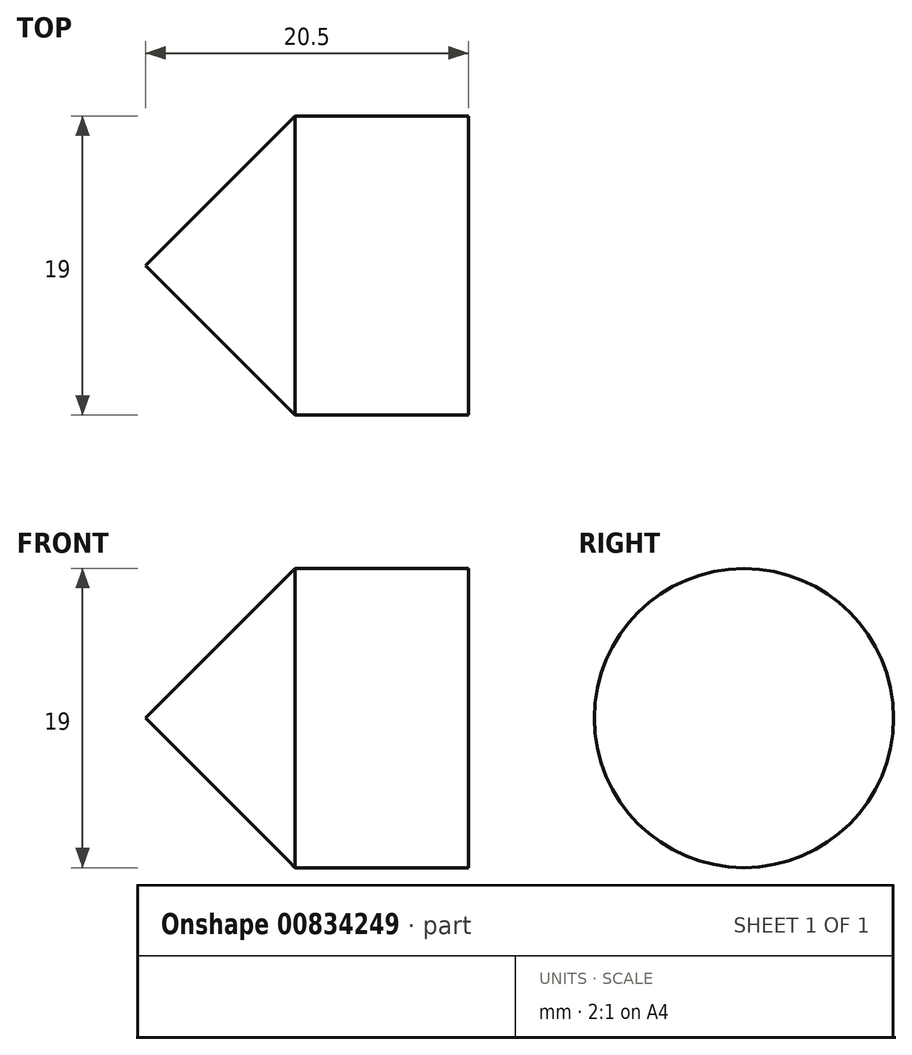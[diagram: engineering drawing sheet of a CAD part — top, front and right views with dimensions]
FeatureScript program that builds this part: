
annotation { "Feature Type Name" : "Feature", "Feature Type Description" : "" }
export const myFeature = defineFeature(function(context is Context, id is Id, definition is map)
    precondition{}
    {
        {
            var Q0;
            Q0=qCreatedBy(makeId("Front.planeOp"),FACE);
            var sketch = newSketch(context, id + "F0", { "sketchPlane" : qUnion([Q0])});
            skLineSegment(sketch, "E0", {"start": v(0, 0) * mm, "end": v(-9.5, 0) * mm});
            skLineSegment(sketch, "E1", {"start": v(-9.5, 0) * mm, "end": v(0, 9.5) * mm});
            skLineSegment(sketch, "E2", {"start": v(0, 9.5) * mm, "end": v(0, 0) * mm});
            skLineSegment(sketch, "E3", {"start": v(-20.98, 0) * mm, "end": v(26.86, 0) * mm, "construction": true});
            skLineSegment(sketch, "E4", {"start": v(0, 0) * mm, "end": v(11, 0) * mm});
            skLineSegment(sketch, "E5", {"start": v(11, 0) * mm, "end": v(11, 9.5) * mm});
            skLineSegment(sketch, "E6", {"start": v(11, 9.5) * mm, "end": v(0, 9.5) * mm});
            skSolve(sketch);
        }
        {
            var Q0;
            Q0=makeQuery(id+"F0.imprint","IMPRINT",FACE,{"disambiguationData":[TD([[makeQuery(id+"F0.imprint","IMPRINT",EDGE,{"derivedFrom":sQuery(id+"F0.wireOp",EDGE,"E0")}),-1.0]])]});
            var Q1;
            Q1=makeQuery(id+"F0.imprint","IMPRINT",FACE,{"disambiguationData":[TD([[makeQuery(id+"F0.imprint","IMPRINT",EDGE,{"derivedFrom":sQuery(id+"F0.wireOp",EDGE,"E2")}),1.0]])]});
            var Q2;
            Q2=sQuery(id+"F0.wireOp",EDGE,"E3");
            revolve(context, id + "F1", {"surfaceOperationType" : NewSurfaceOperationType.NEW, "entities" : qUnion([Q0, Q1]), "axis" : qUnion([Q2]), "revolveType" : RevolveType.FULL});
        }
    });
